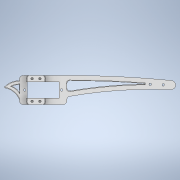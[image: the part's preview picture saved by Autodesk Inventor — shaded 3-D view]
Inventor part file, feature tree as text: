
AUTODESK INVENTOR PART (.ipt)
format: ipt  version: 2020.3 (Build 243373000, 373)  size: 330,752 bytes
history: native  units: mm
features: fillet x7, hole x3, sketch x2, extrude x2, chamfer x1
ambient origin geometry x8: Origin, YZ Plane, XZ Plane, XY Plane, X Axis, Y Axis, Z Axis, Center Point
bodies: Solid1 (feature_tree)
feature tree (15):
  sketch  "Sketch1"  dims[d4=6.0mm d5=24.6mm d6=12.4mm d7=5.0mm d15=7.0mm]
  extrude  "Extrusion1"  Depth=24.6mm
  fillet  "Fillet1"  Radius=12.4mm
  fillet  "Fillet2"  Radius=5.0mm
  fillet  "Fillet3"  Radius=7.0mm
  hole  "Hole1"  [1 undecoded]
  fillet  "Fillet4"  Radius=20.0mm
  hole  "Hole2"  [1 undecoded]
  extrude  "Extrusion3"  Depth=10.0mm
  sketch  "Sketch3"  dims[d17=6.0mm d18=4.0mm d21=20.0mm d23=80.0mm d24=15.0mm d29=29.670597mm d30=6.0mm d31=10.0mm d33=6.0mm d34=0.0mm d40=3.0mm d41=3.0mm d42=2.0mm d43=4.0mm d44=3.0mm d45=4.0mm d50=13.0mm d51=12.0mm d52=22.68928mm d53=16.057029mm d54=2.0mm d55=50.8mm d56=4.0mm d57=2.0mm d58=90.0deg d59=8.0mm d60=20.594885mm d61=0.5mm d62=2.0mm d63=4.0mm d64=4.0mm d65=2.0mm d66=90.0deg d67=8.0mm d68=20.594885mm d69=20.92mm d70=0.0mm d71=2.0mm d80=2.0mm d81=2.0mm d82=45.0deg d87=0.5mm d88=0.5mm d89=6.8mm d90=28.4mm d91=6.0mm d99=2.0mm d100=6.0mm d101=4.0mm d102=2.0mm d103=90.0deg d104=10.0mm d105=20.594885mm]
  hole  "Hole5"  [1 undecoded]
  fillet  "Fillet5"  Radius=6.0mm
  chamfer  "Chamfer2"  Distance=10.0mm
  fillet  "Fillet8"  Radius=6.0mm
  fillet  "Fillet9"  Radius=3.0mm
note: 3 required parameter values undecoded (feature->parameter linkage not recoverable at this tier; creation-order binding heuristic only, values carry confidence <= 0.55)
